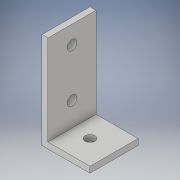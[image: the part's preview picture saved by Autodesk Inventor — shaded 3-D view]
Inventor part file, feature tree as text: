
AUTODESK INVENTOR PART (.ipt)
format: ipt  version: 2018 (Build 220112000, 112)  size: 118,272 bytes
history: native  units: in
note: dims shown in document units (in); Inventor stores cm internally (conversion verified against a paired STEP export)
features: extrude x3, sketch x3
ambient origin geometry x8: Origin, YZ Plane, XZ Plane, XY Plane, X Axis, Y Axis, Z Axis, Center Point
bodies: Solid1 (feature_tree)
feature tree (6):
  extrude  "Extrusion1"  Depth=2.0in
  extrude  "Extrusion2"  Depth=0.125in
  extrude  "Extrusion3"  Depth=1.0in
  sketch  "Sketch1"  dims[d0=0.125in d1=2.0in]
  sketch  "Sketch2"  dims[d2=1.0in d3=0.125in]
  sketch  "Sketch3"  dims[d4=1.0in d5=0.0in d6=0.625in d7=1.0in d8=0.2031in d9=0.2031in d10=1.0in d11=0.0in d12=0.5in d13=0.2031in d14=1.0in d15=0.0in]
